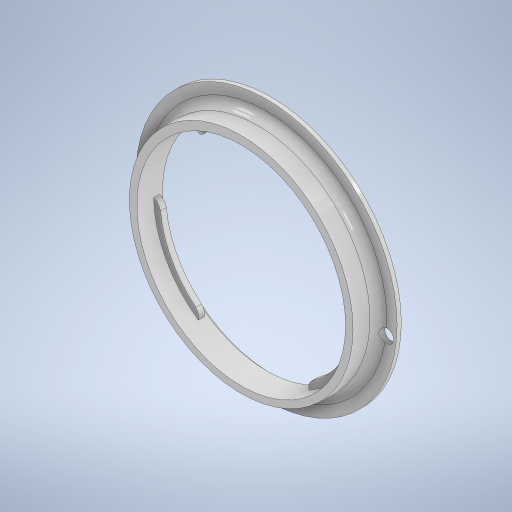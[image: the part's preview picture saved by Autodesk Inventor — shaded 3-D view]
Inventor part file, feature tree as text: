
AUTODESK INVENTOR PART (.ipt)
format: ipt  version: 2023 (Build 270158000, 158)  size: 879,104 bytes
history: native  units: mm
features: extrude x8, other x2, sketch x1, fillet x1
ambient origin geometry x8: Origin, YZ Plane, XZ Plane, XY Plane, X Axis, Y Axis, Z Axis, Center Point
bodies: Body1 (feature_tree)
feature tree (12):
  other  "CE2_adaptor_thin_2_v7"
  sketch  "Schizzo6"
  extrude  "Estrusione7"  Depth=1.0mm TaperAngle=0.0deg
  extrude  "Estrusione8"  Depth=7.0mm TaperAngle=0.0deg
  extrude  "Estrusione9"  Depth=3.0mm TaperAngle=0.0deg
  extrude  "Estrusione10"  Depth=4.75mm TaperAngle=0.0deg
  extrude  "Estrusione11"  Depth=3.0mm TaperAngle=0.0deg
  extrude  "Estrusione12"  Depth=1.6mm TaperAngle=0.0deg
  extrude  "Estrusione13"  Depth=1.6mm TaperAngle=0.0deg
  extrude  "Estrusione14"  Depth=0.9mm TaperAngle=0.0deg
  fillet  "Raccordo3"  Radius=53.0mm
  other  "Lavorazione mesh1"
